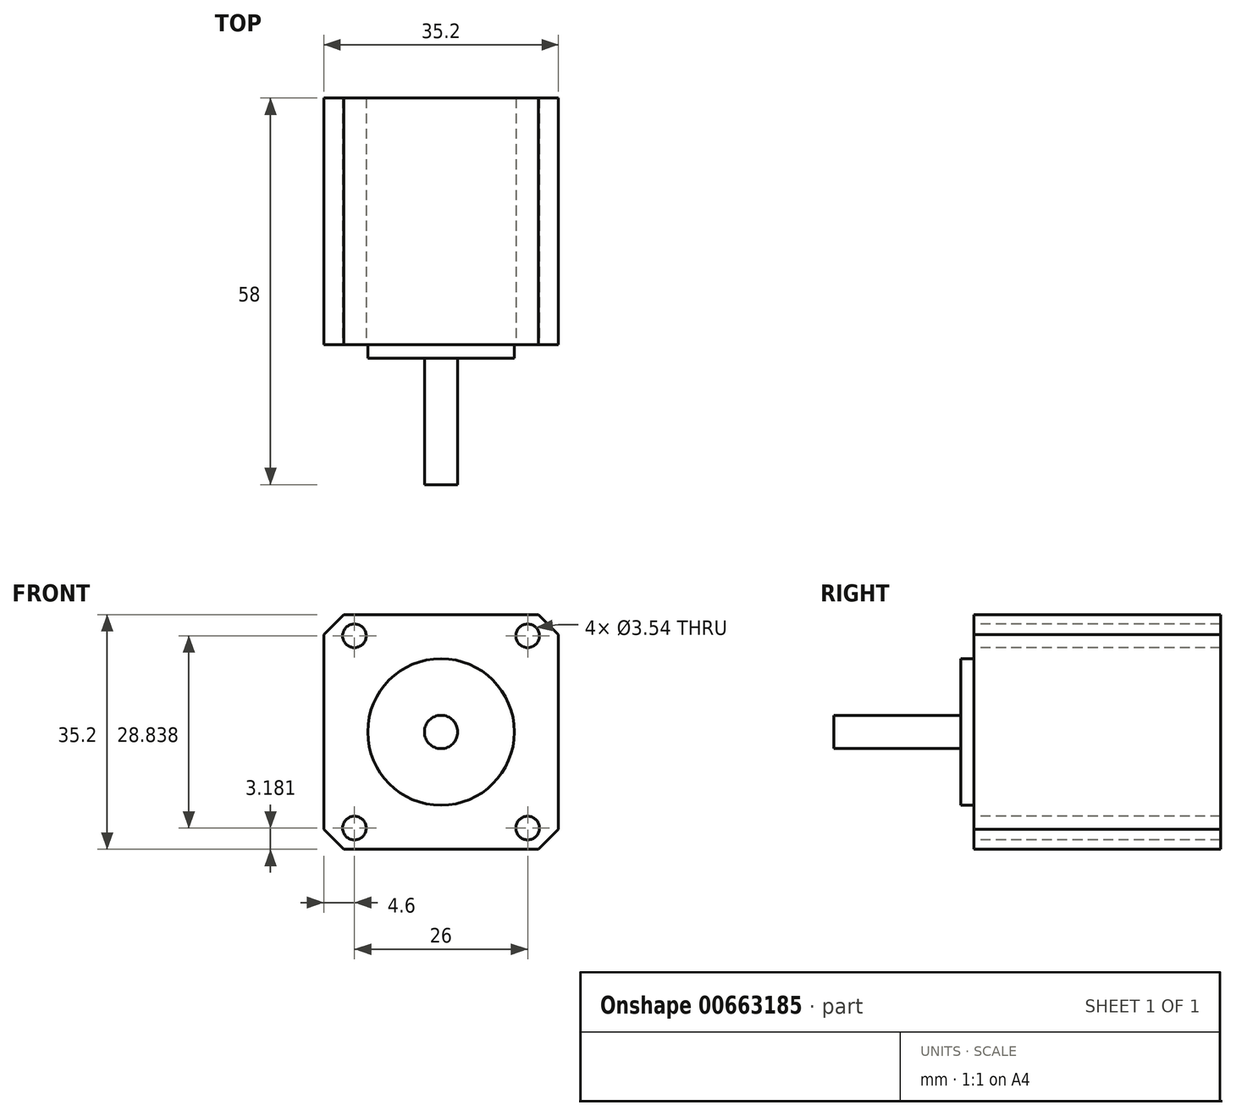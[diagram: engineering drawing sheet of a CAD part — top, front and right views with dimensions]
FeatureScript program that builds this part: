
annotation { "Feature Type Name" : "Feature", "Feature Type Description" : "" }
export const myFeature = defineFeature(function(context is Context, id is Id, definition is map)
    precondition{}
    {
        {
            var Q0;
            Q0=qCreatedBy(makeId("Front.planeOp"),FACE);
            var sketch = newSketch(context, id + "F0", { "sketchPlane" : qUnion([Q0])});
            skLineSegment(sketch, "E0.bottom", {"start": v(-17.6, 17.6) * mm, "end": v(17.6, 17.6) * mm});
            skLineSegment(sketch, "E0.top", {"start": v(-17.6, -17.6) * mm, "end": v(17.6, -17.6) * mm});
            skLineSegment(sketch, "E0.left", {"start": v(-17.6, 17.6) * mm, "end": v(-17.6, -17.6) * mm});
            skLineSegment(sketch, "E0.right", {"start": v(17.6, 17.6) * mm, "end": v(17.6, -17.6) * mm});
            skCircle(sketch, "E1", {"center": v(0, 0) * mm, "radius": 11 * mm});
            skCircle(sketch, "E2", {"center": v(0, 0) * mm, "radius": 2.5 * mm});
            skCircle(sketch, "E3", {"center": v(13, 14.42) * mm, "radius": 1.77 * mm});
            skCircle(sketch, "E4.MirrorC", {"center": v(-13, 14.42) * mm, "radius": 1.77 * mm});
            skCircle(sketch, "E5.MirrorC", {"center": v(13, -14.42) * mm, "radius": 1.77 * mm});
            skCircle(sketch, "E6.MirrorC", {"center": v(-13, -14.42) * mm, "radius": 1.77 * mm});
            skLineSegment(sketch, "E7.MirrorCS", {"start": v(17.6, -17.6) * mm, "end": v(17.6, 17.6) * mm});
            skSolve(sketch);
        }
        {
            var Q0;
            Q0=makeQuery(id+"F0.imprint","IMPRINT",FACE,{"disambiguationData":[TD([[makeQuery(id+"F0.imprint","IMPRINT",EDGE,{"derivedFrom":sQuery(id+"F0.wireOp",EDGE,"E0.bottom")}),-1.0]])]});
            var Q1;
            Q1=makeQuery(id+"F0.imprint","IMPRINT",FACE,{"disambiguationData":[TD([[makeQuery(id+"F0.imprint","IMPRINT",EDGE,{"derivedFrom":sQuery(id+"F0.wireOp",EDGE,"E1")}),1.0]])]});
            var Q2;
            Q2=makeQuery(id+"F0.imprint","IMPRINT",FACE,{"disambiguationData":[TD([[makeQuery(id+"F0.imprint","IMPRINT",EDGE,{"derivedFrom":sQuery(id+"F0.wireOp",EDGE,"E2")}),1.0]])]});
            extrude(context, id + "F1", {"entities" : qUnion([Q0, Q1, Q2]), "oppositeDirection" : true, "depth" : 37 * mm, "offsetDistance" : 25 * mm});
        }
        {
            var Q0;
            Q0=makeQuery(id+"F0.imprint","IMPRINT",FACE,{"disambiguationData":[TD([[makeQuery(id+"F0.imprint","IMPRINT",EDGE,{"derivedFrom":sQuery(id+"F0.wireOp",EDGE,"E1")}),1.0]])]});
            extrude(context, id + "F2", {"entities" : qUnion([Q0]), "operationType" : NewBodyOperationType.ADD, "depth" : 2 * mm, "offsetDistance" : 25 * mm});
        }
        {
            var Q0;
            Q0=makeQuery(id+"F0.imprint","IMPRINT",FACE,{"disambiguationData":[TD([[makeQuery(id+"F0.imprint","IMPRINT",EDGE,{"derivedFrom":sQuery(id+"F0.wireOp",EDGE,"E2")}),1.0]])]});
            extrude(context, id + "F3", {"entities" : qUnion([Q0]), "operationType" : NewBodyOperationType.ADD, "depth" : 21 * mm, "offsetDistance" : 25 * mm});
        }
        {
            var Q0;
            Q0=makeQuery(id+"F1.opExtrude","SWEPT_EDGE",EDGE,{"disambiguationData":[OSD([sQuery(id+"F0.wireOp",EDGE,"E0.bottom"),sQuery(id+"F0.wireOp",EDGE,"E0.right")])]});
            var Q1;
            Q1=makeQuery(id+"F1.opExtrude","SWEPT_EDGE",EDGE,{"disambiguationData":[OSD([sQuery(id+"F0.wireOp",EDGE,"E0.bottom"),sQuery(id+"F0.wireOp",EDGE,"E0.left")])]});
            var Q2;
            Q2=makeQuery(id+"F1.opExtrude","SWEPT_EDGE",EDGE,{"disambiguationData":[OSD([sQuery(id+"F0.wireOp",EDGE,"E0.top"),sQuery(id+"F0.wireOp",EDGE,"E0.right")])]});
            var Q3;
            Q3=makeQuery(id+"F1.opExtrude","SWEPT_EDGE",EDGE,{"disambiguationData":[OSD([sQuery(id+"F0.wireOp",EDGE,"E0.top"),sQuery(id+"F0.wireOp",EDGE,"E0.left")])]});
            chamfer(context, id + "F4", {"entities" : qUnion([Q0, Q1, Q2, Q3]), "width" : 3 * mm, "tangentPropagation" : true});
        }
    });
